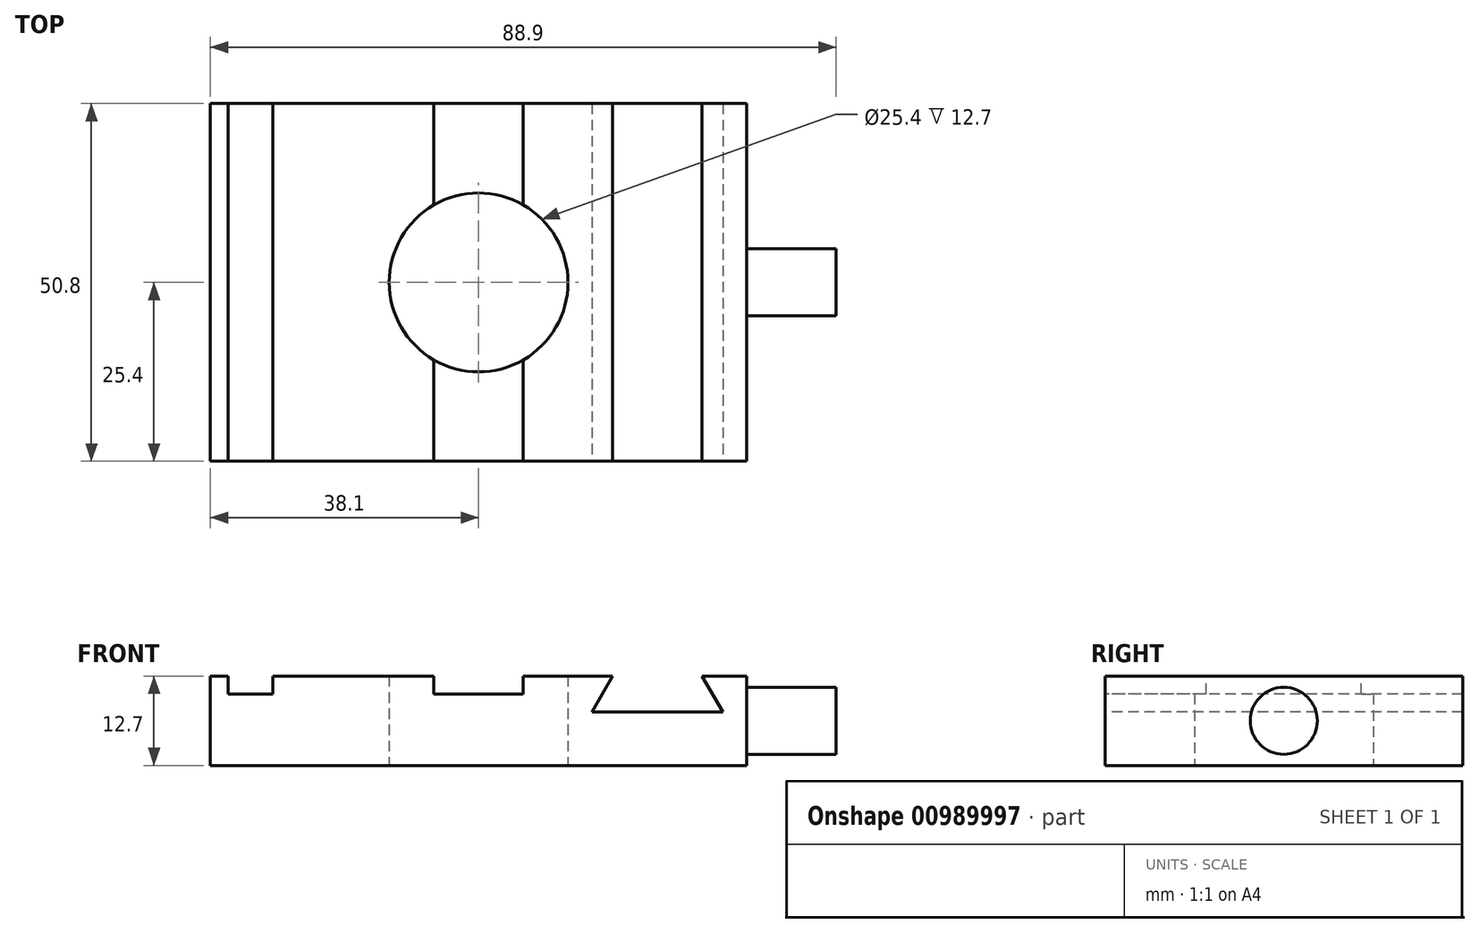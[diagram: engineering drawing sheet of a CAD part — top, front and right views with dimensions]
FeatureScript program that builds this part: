
annotation { "Feature Type Name" : "Feature", "Feature Type Description" : "" }
export const myFeature = defineFeature(function(context is Context, id is Id, definition is map)
    precondition{}
    {
        {
            var Q0;
            Q0=qCreatedBy(makeId("Top.planeOp"),FACE);
            var sketch = newSketch(context, id + "F0", { "sketchPlane" : qUnion([Q0])});
            skLineSegment(sketch, "E0.bottom", {"start": v(38.1, -25.4) * mm, "end": v(-38.1, -25.4) * mm});
            skLineSegment(sketch, "E0.top", {"start": v(38.1, 25.4) * mm, "end": v(-38.1, 25.4) * mm});
            skLineSegment(sketch, "E0.left", {"start": v(38.1, -25.4) * mm, "end": v(38.1, 25.4) * mm});
            skLineSegment(sketch, "E0.right", {"start": v(-38.1, -25.4) * mm, "end": v(-38.1, 25.4) * mm});
            skPoint(sketch, "E0.middle", {"position": v(0, 0) * mm});
            skCircle(sketch, "E1", {"center": v(0, 0) * mm, "radius": 12.7 * mm});
            skSolve(sketch);
        }
        {
            var Q0;
            Q0=makeQuery(id+"F0.imprint","IMPRINT",FACE,{"disambiguationData":[TD([[makeQuery(id+"F0.imprint","IMPRINT",EDGE,{"derivedFrom":sQuery(id+"F0.wireOp",EDGE,"E0.bottom")}),-1.0]])]});
            extrude(context, id + "F1", {"entities" : qUnion([Q0]), "depth" : 12.7 * mm, "offsetDistance" : 25.4 * mm});
        }
        {
            var Q0;
            Q0=makeQuery(id+"F1.opExtrude","CAP_FACE",FACE,{"disambiguationData":[OSD([sQuery(id+"F0.wireOp",EDGE,"E0.bottom"),sQuery(id+"F0.wireOp",EDGE,"E0.top"),sQuery(id+"F0.wireOp",EDGE,"E0.left"),sQuery(id+"F0.wireOp",EDGE,"E0.right"),sQuery(id+"F0.wireOp",EDGE,"E1")])],"isStart":false});
            var sketch = newSketch(context, id + "F2", { "sketchPlane" : qUnion([Q0])});
            skLineSegment(sketch, "E2.bottom", {"start": v(-35.56, 25.4) * mm, "end": v(-29.21, 25.4) * mm});
            skLineSegment(sketch, "E2.top", {"start": v(-35.56, -25.4) * mm, "end": v(-29.21, -25.4) * mm});
            skLineSegment(sketch, "E2.left", {"start": v(-29.21, 25.4) * mm, "end": v(-29.21, -25.4) * mm});
            skLineSegment(sketch, "E2.right", {"start": v(-35.56, 25.4) * mm, "end": v(-35.56, -25.4) * mm});
            skLineSegment(sketch, "E3", {"start": v(-6.35, 25.4) * mm, "end": v(-6.35, -25.4) * mm});
            skLineSegment(sketch, "E4", {"start": v(-6.35, -25.4) * mm, "end": v(6.35, -25.4) * mm});
            skLineSegment(sketch, "E5", {"start": v(6.35, -25.4) * mm, "end": v(6.35, 25.4) * mm});
            skLineSegment(sketch, "E6", {"start": v(0, -25.4) * mm, "end": v(0, 25.4) * mm, "construction": true});
            skSolve(sketch);
        }
        {
            var Q0;
            Q0=makeQuery(id+"F2.imprint","IMPRINT",FACE,{"disambiguationData":[TD([[makeQuery(id+"F2.imprint","IMPRINT",EDGE,{"derivedFrom":sQuery(id+"F2.wireOp",EDGE,"E2.bottom")}),1.0]])]});
            var Q1;
            {var subQ0=sQuery(id+"F2.wireOp",EDGE,"E3");var subQ1=makeQuery(id+"F1.opExtrude","CAP_EDGE",EDGE,{"disambiguationData":[OSD([sQuery(id+"F0.wireOp",EDGE,"E0.top")])],"isStart":false});var subQ2=makeQuery(id+"F2.imprint","INTERSECT",VERTEX,{"derivedFrom":[subQ1,subQ0]});Q1=makeQuery(id+"F2.imprint","IMPRINT",FACE,{"disambiguationData":[TD([[makeQuery(id+"F2.imprint","IMPRINT",EDGE,{"disambiguationData":[TD([[subQ2,-1.0]])],"derivedFrom":subQ0}),1.0]])]});}
            var Q2;
            {var subQ0=sQuery(id+"F2.wireOp",EDGE,"E4");Q2=makeQuery(id+"F2.imprint","IMPRINT",FACE,{"disambiguationData":[TD([[makeQuery(id+"F2.imprint","IMPRINT",EDGE,{"derivedFrom":subQ0}),-1.0]])]});}
            extrude(context, id + "F3", {"entities" : qUnion([Q0, Q1, Q2]), "operationType" : NewBodyOperationType.REMOVE, "oppositeDirection" : true, "depth" : 2.54 * mm, "offsetDistance" : 25.4 * mm});
        }
        {
            var Q0;
            Q0=makeQuery(id+"F1.opExtrude","SWEPT_FACE",FACE,{"disambiguationData":[OSD([sQuery(id+"F0.wireOp",EDGE,"E0.bottom")])]});
            var sketch = newSketch(context, id + "F4", { "sketchPlane" : qUnion([Q0])});
            skLineSegment(sketch, "E7", {"start": v(19.05, 12.7) * mm, "end": v(16.12, 7.62) * mm});
            skLineSegment(sketch, "E8", {"start": v(16.12, 7.62) * mm, "end": v(34.68, 7.62) * mm});
            skLineSegment(sketch, "E9", {"start": v(34.68, 7.62) * mm, "end": v(31.75, 12.7) * mm});
            skLineSegment(sketch, "E10", {"start": v(31.75, 12.7) * mm, "end": v(19.05, 12.7) * mm});
            skLineSegment(sketch, "E11", {"start": v(25.4, 7.62) * mm, "end": v(25.4, 12.7) * mm, "construction": true});
            skSolve(sketch);
        }
        {
            var Q0;
            Q0=makeQuery(id+"F4.imprint","IMPRINT",FACE,{"disambiguationData":[TD([[makeQuery(id+"F4.imprint","IMPRINT",EDGE,{"derivedFrom":sQuery(id+"F4.wireOp",EDGE,"E7")}),1.0]])]});
            extrude(context, id + "F5", {"entities" : qUnion([Q0]), "operationType" : NewBodyOperationType.REMOVE, "endBound" : BoundingType.THROUGH_ALL, "oppositeDirection" : true, "depth" : 25.4 * mm, "offsetDistance" : 25.4 * mm});
        }
        {
            var Q0;
            Q0=makeQuery(id+"F1.opExtrude","SWEPT_FACE",FACE,{"disambiguationData":[OSD([sQuery(id+"F0.wireOp",EDGE,"E0.left")])]});
            var sketch = newSketch(context, id + "F6", { "sketchPlane" : qUnion([Q0])});
            skCircle(sketch, "E12", {"center": v(0, 6.35) * mm, "radius": 4.76 * mm});
            skPoint(sketch, "E12.centerSnap0", {"position": v(-25.4, 6.35) * mm});
            skPoint(sketch, "E12.centerSnap1", {"position": v(0, 12.7) * mm});
            skSolve(sketch);
        }
        {
            var Q0;
            Q0=makeQuery(id+"F6.imprint","IMPRINT",FACE,{"disambiguationData":[TD([[makeQuery(id+"F6.imprint","IMPRINT",EDGE,{"derivedFrom":sQuery(id+"F6.wireOp",EDGE,"E12")}),1.0]])]});
            extrude(context, id + "F7", {"entities" : qUnion([Q0]), "operationType" : NewBodyOperationType.ADD, "depth" : 12.7 * mm, "offsetDistance" : 25.4 * mm});
        }
    });
